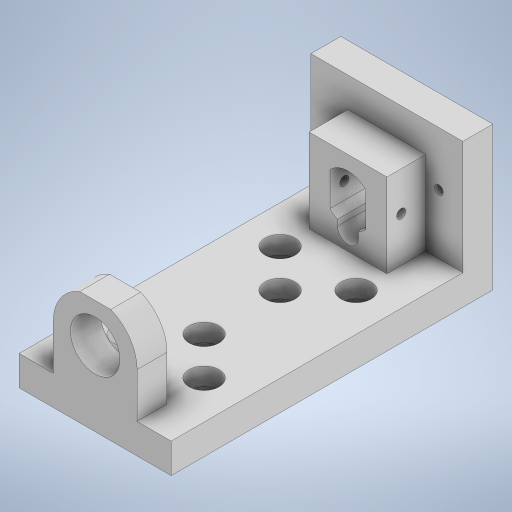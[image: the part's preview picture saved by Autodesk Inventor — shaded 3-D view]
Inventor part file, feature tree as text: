
AUTODESK INVENTOR PART (.ipt)
format: ipt  version: 2024 (Build 280153000, 153)  size: 454,144 bytes
history: native  units: mm
features: projected_geometry x11, extrude x10, sketch x10, plane x1, fillet x1
ambient origin geometry x8: Origin, YZ Plane, XZ Plane, XY Plane, X Axis, Y Axis, Z Axis, Center Point
bodies: Solid1 (feature_tree)
feature tree (33):
  extrude  "Extrusion1"  Depth=6.0mm
  extrude  "Extrusion2"  Depth=10.0mm
  extrude  "Extrusion3"  Depth=10.0mm
  plane  "Work Plane1"
  extrude  "Extrusion4"  Depth=10.0mm
  extrude  "Extrusion5"  TaperAngle=0.0deg  [1 undecoded]
  extrude  "Extrusion6"  Depth=26.0mm
  extrude  "Extrusion7"  Depth=5.0mm
  extrude  "Extrusion8"  Depth=10.0mm TaperAngle=0.0deg
  extrude  "Extrusion9"  TaperAngle=0.0deg  [1 undecoded]
  extrude  "Extrusion10"  TaperAngle=0.0deg  [1 undecoded]
  fillet  "Fillet1"  [1 undecoded]
  sketch  "Sketch1"  dims[d1=4.0mm d2=6.0mm]
  sketch  "Sketch2"  dims[d3=28.0mm d4=10.0mm]
  projected_geometry  "Projected Loop1"
  sketch  "Sketch3"  dims[d5=50.8mm d6=10.0mm]
  projected_geometry  "Projected Loop2"
  sketch  "Sketch4"  dims[d7=0.0mm d8=10.0mm]
  projected_geometry  "Projected Loop3"
  sketch  "Sketch5"  dims[d9=87.5mm d10=0.0mm d12=0.0mm]
  projected_geometry  "Projected Loop4"
  sketch  "Sketch6"  dims[d13=26.0mm d14=26.0mm]
  projected_geometry  "Projected Loop5"
  sketch  "Sketch7"  dims[d15=5.0mm d17=5.0mm]
  projected_geometry  "Projected Loop6"
  projected_geometry  "Projected Loop7"
  projected_geometry  "Projected Loop8"
  sketch  "Sketch8"  dims[d19=10.0mm d20=13.0mm d21=0.0mm]
  projected_geometry  "Projected Loop9"
  sketch  "Sketch9"  dims[d22=0.0mm d23=0.0mm]
  projected_geometry  "Projected Loop10"
  sketch  "Sketch10"  dims[d24=16.5mm d25=12.0mm d26=0.0mm d27=0.0mm d28=7.0mm d29=0.0mm d31=7.0mm d32=16.5mm d33=-13.0mm d34=0.0mm d35=8.25mm d36=3.0mm d37=26.0mm d38=0.0mm d39=35.7mm d40=0.0mm d41=6.35mm d42=12.7mm d43=12.7mm d44=12.7mm d45=12.7mm d46=12.7mm d47=26.0mm d48=0.0mm d49=0.0mm d50=8.0mm d51=8.0mm d52=2.84mm d53=26.0mm d54=0.0mm d55=28.0mm d56=16.5mm d57=6.0mm d58=6.0mm d59=10.0mm d60=0.0mm d61=10.0mm d62=10.0mm d63=10.0mm d64=10.0mm d65=10.0mm d66=10.0mm d67=6.0mm d68=0.0mm d69=10.0mm d70=10.0mm d71=5.0mm d72=0.0mm d73=6.35mm d74=6.35mm d75=7.0mm d76=5.5mm d77=0.0mm d78=7.0mm d79=5.5mm d80=0.0mm d81=0.0mm d82=2.0mm]
  projected_geometry  "Projected Loop11"
note: 4 required parameter values undecoded (feature->parameter linkage not recoverable at this tier; creation-order binding heuristic only, values carry confidence <= 0.55)
